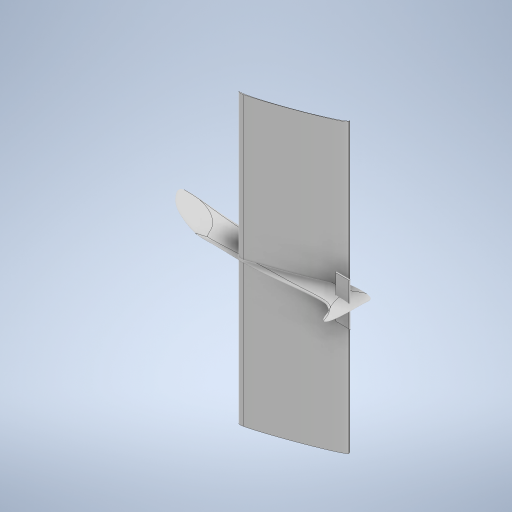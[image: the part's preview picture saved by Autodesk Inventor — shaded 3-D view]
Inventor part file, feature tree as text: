
AUTODESK INVENTOR PART (.ipt)
format: ipt  version: 2024 (Build 280153000, 153)  size: 726,528 bytes
history: native  units: mm
features: other x3, extrude x2, fillet x1
ambient origin geometry x8: Origin, YZ Plane, XZ Plane, XY Plane, X Axis, Y Axis, Z Axis, Center Point
bodies: Body1 (feature_tree), Body2 (feature_tree)
feature tree (6):
  other  "ソリッド1"
  extrude  "押し出し1"  Depth=1.047198mm TaperAngle=0.0deg
  extrude  "押し出し2"  Depth=150.0mm TaperAngle=0.0deg
  other  "フォーム2"
  fillet  "フィレット11"  Radius=3.490659mm
  other  "ソリッド2"
